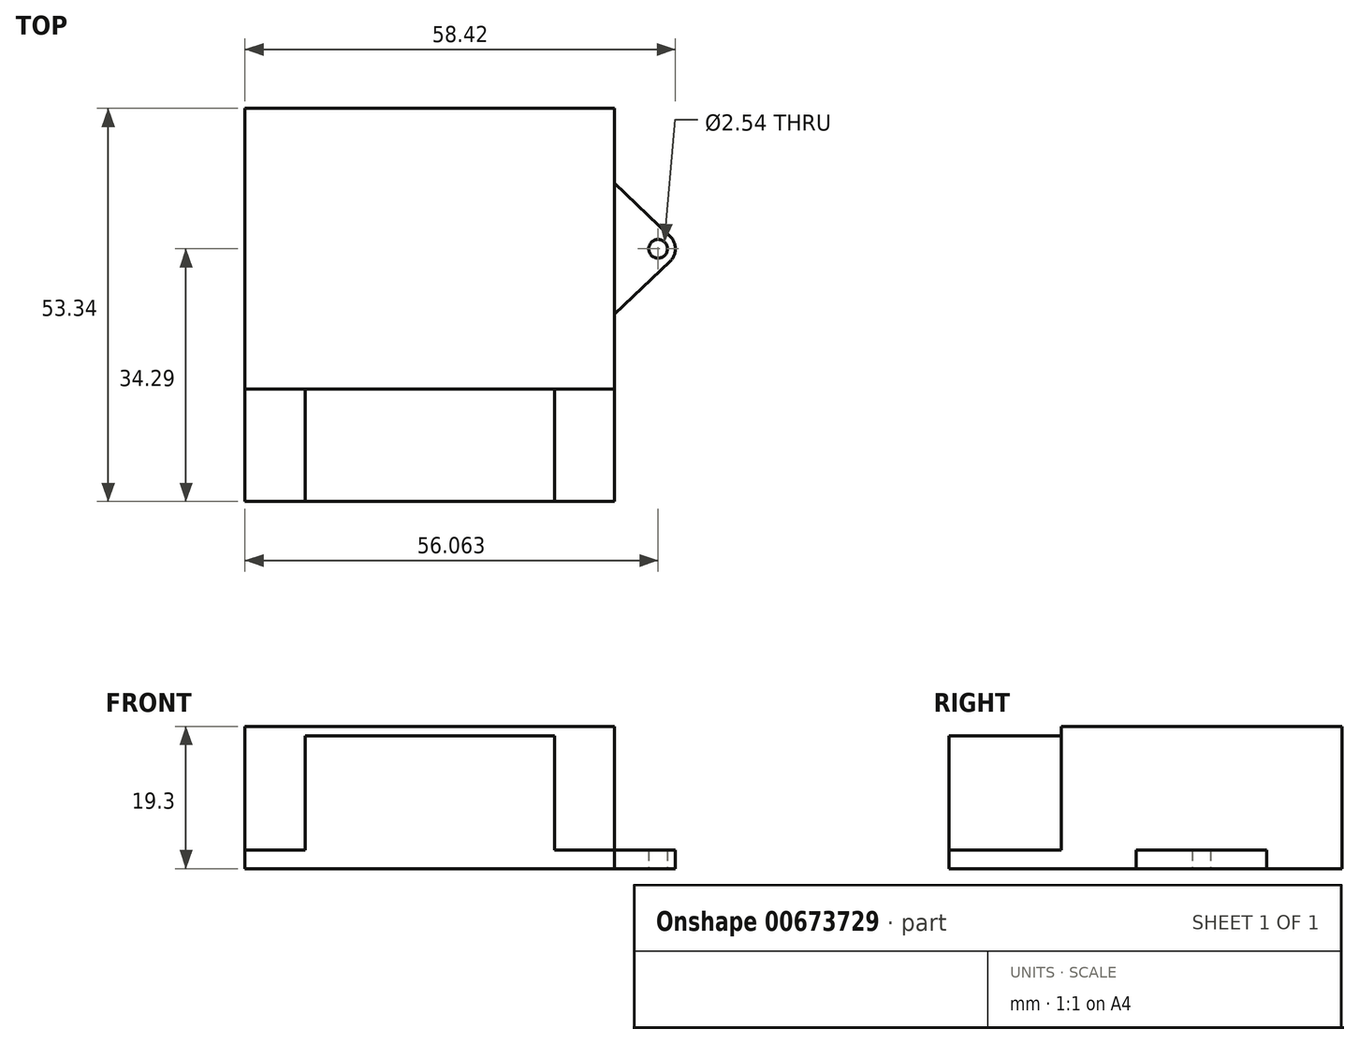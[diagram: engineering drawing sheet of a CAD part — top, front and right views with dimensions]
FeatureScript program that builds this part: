
annotation { "Feature Type Name" : "Feature", "Feature Type Description" : "" }
export const myFeature = defineFeature(function(context is Context, id is Id, definition is map)
    precondition{}
    {
        {
            var Q0;
            Q0=qCreatedBy(makeId("Top.planeOp"),FACE);
            var sketch = newSketch(context, id + "F0", { "sketchPlane" : qUnion([Q0])});
            skLineSegment(sketch, "E0.bottom", {"start": v(25.08, 19.05) * mm, "end": v(-25.08, 19.05) * mm});
            skLineSegment(sketch, "E0.top", {"start": v(25.08, -19.05) * mm, "end": v(-25.08, -19.05) * mm});
            skLineSegment(sketch, "E0.left", {"start": v(25.08, 19.05) * mm, "end": v(25.08, -19.05) * mm});
            skLineSegment(sketch, "E0.right", {"start": v(-25.08, 19.05) * mm, "end": v(-25.08, -19.05) * mm});
            skPoint(sketch, "E0.middle", {"position": v(0, 0) * mm});
            skLineSegment(sketch, "E1.bottom", {"start": v(-25.08, -19.05) * mm, "end": v(25.08, -19.05) * mm});
            skLineSegment(sketch, "E1.top", {"start": v(-25.08, -34.3) * mm, "end": v(25.08, -34.3) * mm});
            skLineSegment(sketch, "E1.left", {"start": v(-25.08, -19.05) * mm, "end": v(-25.08, -34.3) * mm});
            skLineSegment(sketch, "E1.right", {"start": v(25.08, -19.05) * mm, "end": v(25.08, -34.3) * mm});
            skLineSegment(sketch, "E2.bottom", {"start": v(-16.92, -34.3) * mm, "end": v(16.92, -34.3) * mm});
            skLineSegment(sketch, "E2.top", {"start": v(-16.92, -19.05) * mm, "end": v(16.92, -19.05) * mm});
            skLineSegment(sketch, "E2.left", {"start": v(-16.92, -34.3) * mm, "end": v(-16.92, -19.05) * mm});
            skLineSegment(sketch, "E2.right", {"start": v(16.92, -34.3) * mm, "end": v(16.92, -19.05) * mm});
            skLineSegment(sketch, "E3", {"start": v(0, -34.3) * mm, "end": v(0, -19.05) * mm, "construction": true});
            skLineSegment(sketch, "E4", {"start": v(25.08, -8.9) * mm, "end": v(32.6, -1.7) * mm});
            skLineSegment(sketch, "E5", {"start": v(32.6, -1.7) * mm, "end": v(32.6, 1.7) * mm, "construction": true});
            skLineSegment(sketch, "E6", {"start": v(32.6, 1.7) * mm, "end": v(25.08, 8.9) * mm});
            skArc(sketch, "E7", {"start": v(32.6, -1.7) * mm, "mid": v(33.34, 0) * mm, "end": v(32.6, 1.7) * mm});
            skLineSegment(sketch, "E8", {"start": v(32.6, 0) * mm, "end": v(25.08, 0) * mm, "construction": true});
            skCircle(sketch, "E9", {"center": v(30.98, 0) * mm, "radius": 1.27 * mm});
            skLineSegment(sketch, "E10", {"start": v(0, 0) * mm, "end": v(0, 19.05) * mm, "construction": true});
            skLineSegment(sketch, "E11.MirrorCS", {"start": v(-32.6, 0) * mm, "end": v(-25.08, 0) * mm, "construction": true});
            skLineSegment(sketch, "E12.MirrorCS", {"start": v(-32.6, -1.7) * mm, "end": v(-32.6, 1.7) * mm, "construction": true});
            skArc(sketch, "E13.MirrorCS", {"start": v(-32.6, -1.7) * mm, "mid": v(-33.34, 0) * mm, "end": v(-32.6, 1.7) * mm});
            skCircle(sketch, "E14.MirrorC", {"center": v(-30.98, 0) * mm, "radius": 1.27 * mm});
            skLineSegment(sketch, "E15.MirrorCS", {"start": v(-32.6, 1.7) * mm, "end": v(-25.08, 8.9) * mm});
            skLineSegment(sketch, "E16.MirrorCS", {"start": v(-25.08, -8.9) * mm, "end": v(-32.6, -1.7) * mm});
            skSolve(sketch);
        }
        {
            var Q0;
            Q0=makeQuery(id+"F0.imprint","IMPRINT",FACE,{"disambiguationData":[TD([[makeQuery(id+"F0.imprint","IMPRINT",EDGE,{"derivedFrom":sQuery(id+"F0.wireOp",EDGE,"E0.bottom")}),1.0]])]});
            extrude(context, id + "F1", {"entities" : qUnion([Q0]), "depth" : 19.3 * mm, "offsetDistance" : 25.4 * mm});
        }
        {
            var Q0;
            {var subQ2=sQuery(id+"F0.wireOp",EDGE,"E2.left");Q0=makeQuery(id+"F0.imprint","IMPRINT",FACE,{"disambiguationData":[TD([[makeQuery(id+"F0.imprint","IMPRINT",EDGE,{"derivedFrom":subQ2}),-1.0]])]});}
            var Q1;
            Q1=makeQuery(id+"F1.opExtrude","CAP_FACE",FACE,{"disambiguationData":[OSD([sQuery(id+"F0.wireOp",EDGE,"E0.bottom"),sQuery(id+"F0.wireOp",EDGE,"E0.top"),sQuery(id+"F0.wireOp",EDGE,"E0.left"),sQuery(id+"F0.wireOp",EDGE,"E0.right")])],"isStart":false});
            extrude(context, id + "F2", {"entities" : qUnion([Q0]), "operationType" : NewBodyOperationType.ADD, "endBound" : BoundingType.UP_TO_SURFACE, "depth" : 25.4 * mm, "endBoundEntityFace" : qUnion([Q1]), "hasOffset" : true, "offsetDistance" : 1.27 * mm});
        }
        {
            var Q0;
            {var subQ0=sQuery(id+"F0.wireOp",EDGE,"E1.left");Q0=makeQuery(id+"F0.imprint","IMPRINT",FACE,{"disambiguationData":[TD([[makeQuery(id+"F0.imprint","IMPRINT",EDGE,{"derivedFrom":subQ0}),1.0]])]});}
            var Q1;
            {var subQ2=sQuery(id+"F0.wireOp",EDGE,"E1.right");Q1=makeQuery(id+"F0.imprint","IMPRINT",FACE,{"disambiguationData":[TD([[makeQuery(id+"F0.imprint","IMPRINT",EDGE,{"derivedFrom":subQ2}),-1.0]])]});}
            var Q2;
            Q2=makeQuery(id+"F0.imprint","IMPRINT",FACE,{"disambiguationData":[TD([[makeQuery(id+"F0.imprint","IMPRINT",EDGE,{"derivedFrom":sQuery(id+"F0.wireOp",EDGE,"E13.MirrorCS")}),-1.0]])]});
            var Q3;
            {var subQ1=sQuery(id+"F0.wireOp",EDGE,"E4");Q3=makeQuery(id+"F0.imprint","IMPRINT",FACE,{"disambiguationData":[TD([[makeQuery(id+"F0.imprint","IMPRINT",EDGE,{"derivedFrom":subQ1}),1.0]])]});}
            extrude(context, id + "F3", {"entities" : qUnion([Q0, Q1, Q2, Q3]), "operationType" : NewBodyOperationType.ADD, "depth" : 2.54 * mm, "offsetDistance" : 25.4 * mm});
        }
    });
